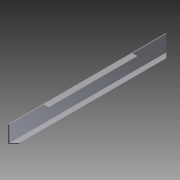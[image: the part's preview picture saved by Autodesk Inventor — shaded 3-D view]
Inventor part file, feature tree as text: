
AUTODESK INVENTOR PART (.ipt)
format: ipt  version: 2012 (Build 160160000, 160)  size: 98,816 bytes
history: native  units: in
note: dims shown in document units (in); Inventor stores cm internally (conversion verified against a paired STEP export)
features: extrude x3, sketch x2
ambient origin geometry x8: Origin, YZ Plane, XZ Plane, XY Plane, X Axis, Y Axis, Z Axis, Center Point
bodies: Solid1 (feature_tree)
feature tree (5):
  extrude  "Extrusion1"  Depth=1.0in
  sketch  "Sketch2"  dims[d2=0.125in d3=0.125in d4=0.125in d5=28.0in d6=0.0in d7=45.0deg d8=0.125in d9=6.0in d10=6.0in d11=28.0in d12=0.0in d13=28.0in d14=0.0in]
  extrude  "Extrusion2"  Depth=0.125in
  extrude  "Extrusion3"  Depth=0.125in
  sketch  "Sketch1"  dims[d0=3.0in d1=1.0in]
